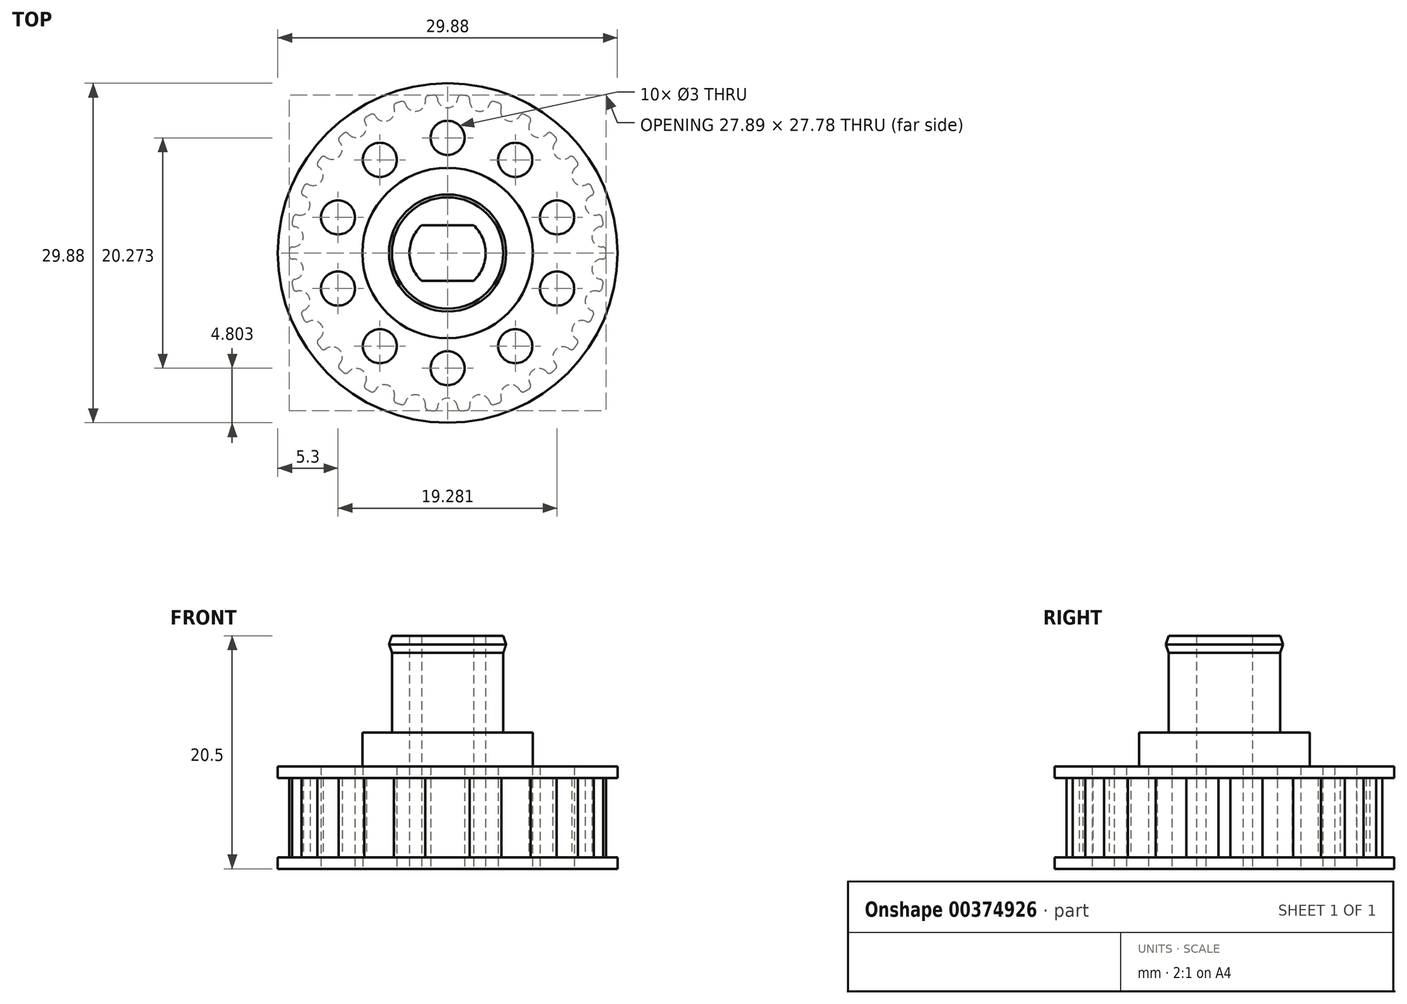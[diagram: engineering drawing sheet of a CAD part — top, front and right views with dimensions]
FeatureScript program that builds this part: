
annotation { "Feature Type Name" : "Feature", "Feature Type Description" : "" }
export const myFeature = defineFeature(function(context is Context, id is Id, definition is map)
    precondition{}
    {
        {
            assignVariable(context, id + "F0", {"name" : "e", "anyValue" : 3});
        }
        {
            assignVariable(context, id + "F1", {"name" : "h1", "anyValue" : 6});
        }
        {
            assignVariable(context, id + "F2", {"name" : "h2", "anyValue" : 6.5 + 5});
        }
        {
            var Q0;
            Q0=qCreatedBy(makeId("Top.planeOp"),FACE);
            var sketch = newSketch(context, id + "F3", { "sketchPlane" : qUnion([Q0])});
            skArc(sketch, "E0", {"start": v(-1.22, 13.89) * mm, "mid": v(0, -13.94) * mm, "end": v(1.22, 13.89) * mm, "construction": true});
            skCircle(sketch, "E1", {"center": v(0, 0) * mm, "radius": 7.5 * mm});
            skCircle(sketch, "E2", {"center": v(0, 0) * mm, "radius": 4.9 * mm});
            skArc(sketch, "E3", {"start": v(-2.28, 2.45) * mm, "mid": v(-3.35, 0) * mm, "end": v(-2.28, -2.45) * mm});
            skLineSegment(sketch, "E4.bottom", {"start": v(2.28, -2.45) * mm, "end": v(-2.28, -2.45) * mm});
            skLineSegment(sketch, "E4.top", {"start": v(2.28, 2.45) * mm, "end": v(-2.28, 2.45) * mm});
            skArc(sketch, "E5.trimOffspring", {"start": v(2.28, -2.45) * mm, "mid": v(3.35, 0) * mm, "end": v(2.28, 2.45) * mm});
            skPoint(sketch, "E6.orphan", {"position": v(3.35, 2.45) * mm});
            skPoint(sketch, "E7.orphan", {"position": v(3.35, -2.45) * mm});
            skPoint(sketch, "E8.orphan", {"position": v(-3.35, -2.45) * mm});
            skPoint(sketch, "E9.orphan", {"position": v(-3.35, 2.45) * mm});
            skLineSegment(sketch, "E10", {"start": v(0, 7.5) * mm, "end": v(0, 12.77) * mm, "construction": true});
            skCircle(sketch, "E11", {"center": v(0, 0) * mm, "radius": 14.94 * mm});
            skCircle(sketch, "E12", {"center": v(0, 10.14) * mm, "radius": 1.5 * mm});
            skCircle(sketch, "E13.1.0", {"center": v(-5.96, 8.2) * mm, "radius": 1.5 * mm});
            skCircle(sketch, "E13.2.0", {"center": v(-9.64, 3.13) * mm, "radius": 1.5 * mm});
            skCircle(sketch, "E13.3.0", {"center": v(-9.64, -3.13) * mm, "radius": 1.5 * mm});
            skCircle(sketch, "E13.4.0", {"center": v(-5.96, -8.2) * mm, "radius": 1.5 * mm});
            skCircle(sketch, "E13.5.0", {"center": v(0, -10.14) * mm, "radius": 1.5 * mm});
            skCircle(sketch, "E13.6.0", {"center": v(5.96, -8.2) * mm, "radius": 1.5 * mm});
            skCircle(sketch, "E13.7.0", {"center": v(9.64, -3.13) * mm, "radius": 1.5 * mm});
            skCircle(sketch, "E13.8.0", {"center": v(9.64, 3.13) * mm, "radius": 1.5 * mm});
            skCircle(sketch, "E13.9.0", {"center": v(5.96, 8.2) * mm, "radius": 1.5 * mm});
            skCircle(sketch, "E14", {"center": v(0, 0) * mm, "radius": 12.77 * mm, "construction": true});
            skLineSegment(sketch, "E15", {"start": v(0, 12.77) * mm, "end": v(0, 14.94) * mm});
            skArc(sketch, "E16", {"start": v(-0.9, 13.61) * mm, "mid": v(0, 12.77) * mm, "end": v(0.9, 13.61) * mm});
            skArc(sketch, "E17", {"start": v(1.22, 13.89) * mm, "mid": v(1, 13.82) * mm, "end": v(0.9, 13.61) * mm});
            skArc(sketch, "E18.MirrorCS", {"start": v(-1.22, 13.89) * mm, "mid": v(-1, 13.82) * mm, "end": v(-0.9, 13.61) * mm});
            skLineSegment(sketch, "E19", {"start": v(0, 0) * mm, "end": v(1.56, 14.86) * mm, "construction": true});
            skLineSegment(sketch, "E20", {"start": v(0, 0) * mm, "end": v(-1.56, 14.86) * mm, "construction": true});
            skArc(sketch, "E21", {"start": v(1.46, 13.87) * mm, "mid": v(1.34, 13.88) * mm, "end": v(1.22, 13.89) * mm});
            skArc(sketch, "E22.trimOffspring", {"start": v(-1.22, 13.89) * mm, "mid": v(-1.34, 13.88) * mm, "end": v(-1.46, 13.87) * mm});
            skArc(sketch, "E23.1.0", {"start": v(-4.08, 13.33) * mm, "mid": v(-4.2, 13.3) * mm, "end": v(-4.3, 13.26) * mm});
            skArc(sketch, "E23.1.1", {"start": v(-4.08, 13.33) * mm, "mid": v(-3.85, 13.3) * mm, "end": v(-3.7, 13.13) * mm});
            skArc(sketch, "E23.1.2", {"start": v(-3.7, 13.13) * mm, "mid": v(-2.66, 12.5) * mm, "end": v(-1.95, 13.5) * mm});
            skArc(sketch, "E23.1.3", {"start": v(-1.7, 13.84) * mm, "mid": v(-1.9, 13.72) * mm, "end": v(-1.95, 13.5) * mm});
            skArc(sketch, "E23.1.4", {"start": v(-1.46, 13.87) * mm, "mid": v(-1.57, 13.85) * mm, "end": v(-1.7, 13.84) * mm});
            skArc(sketch, "E23.2.0", {"start": v(-6.77, 12.2) * mm, "mid": v(-6.87, 12.13) * mm, "end": v(-6.97, 12.07) * mm});
            skArc(sketch, "E23.2.1", {"start": v(-6.77, 12.2) * mm, "mid": v(-6.54, 12.22) * mm, "end": v(-6.36, 12.07) * mm});
            skArc(sketch, "E23.2.2", {"start": v(-6.36, 12.07) * mm, "mid": v(-5.2, 11.67) * mm, "end": v(-4.72, 12.8) * mm});
            skArc(sketch, "E23.2.3", {"start": v(-4.53, 13.19) * mm, "mid": v(-4.7, 13.03) * mm, "end": v(-4.72, 12.8) * mm});
            skArc(sketch, "E23.2.4", {"start": v(-4.3, 13.26) * mm, "mid": v(-4.42, 13.22) * mm, "end": v(-4.53, 13.19) * mm});
            skArc(sketch, "E23.3.0", {"start": v(-9.15, 10.52) * mm, "mid": v(-9.24, 10.44) * mm, "end": v(-9.33, 10.36) * mm});
            skArc(sketch, "E23.3.1", {"start": v(-9.15, 10.52) * mm, "mid": v(-8.93, 10.6) * mm, "end": v(-8.73, 10.48) * mm});
            skArc(sketch, "E23.3.2", {"start": v(-8.73, 10.48) * mm, "mid": v(-7.5, 10.33) * mm, "end": v(-7.27, 11.54) * mm});
            skArc(sketch, "E23.3.3", {"start": v(-7.17, 11.96) * mm, "mid": v(-7.31, 11.77) * mm, "end": v(-7.27, 11.54) * mm});
            skArc(sketch, "E23.3.4", {"start": v(-6.97, 12.07) * mm, "mid": v(-7.07, 12.02) * mm, "end": v(-7.17, 11.96) * mm});
            skArc(sketch, "E23.4.0", {"start": v(-11.14, 8.38) * mm, "mid": v(-11.21, 8.3) * mm, "end": v(-11.28, 8.2) * mm});
            skArc(sketch, "E23.4.1", {"start": v(-11.14, 8.38) * mm, "mid": v(-10.94, 8.5) * mm, "end": v(-10.72, 8.44) * mm});
            skArc(sketch, "E23.4.2", {"start": v(-10.72, 8.44) * mm, "mid": v(-9.5, 8.55) * mm, "end": v(-9.51, 9.77) * mm});
            skArc(sketch, "E23.4.3", {"start": v(-9.5, 10.2) * mm, "mid": v(-9.6, 10) * mm, "end": v(-9.51, 9.77) * mm});
            skArc(sketch, "E23.4.4", {"start": v(-9.33, 10.36) * mm, "mid": v(-9.42, 10.28) * mm, "end": v(-9.5, 10.2) * mm});
            skArc(sketch, "E23.5.0", {"start": v(-12.64, 5.89) * mm, "mid": v(-12.69, 5.78) * mm, "end": v(-12.74, 5.67) * mm});
            skArc(sketch, "E23.5.1", {"start": v(-12.64, 5.89) * mm, "mid": v(-12.47, 6.04) * mm, "end": v(-12.24, 6.03) * mm});
            skArc(sketch, "E23.5.2", {"start": v(-12.24, 6.03) * mm, "mid": v(-11.06, 6.39) * mm, "end": v(-11.34, 7.58) * mm});
            skArc(sketch, "E23.5.3", {"start": v(-11.42, 8) * mm, "mid": v(-11.47, 7.78) * mm, "end": v(-11.34, 7.58) * mm});
            skArc(sketch, "E23.5.4", {"start": v(-11.28, 8.2) * mm, "mid": v(-11.35, 8.1) * mm, "end": v(-11.42, 8) * mm});
            skArc(sketch, "E23.6.0", {"start": v(-13.59, 3.13) * mm, "mid": v(-13.61, 3.01) * mm, "end": v(-13.64, 2.9) * mm});
            skArc(sketch, "E23.6.1", {"start": v(-13.59, 3.13) * mm, "mid": v(-13.45, 3.32) * mm, "end": v(-13.22, 3.35) * mm});
            skArc(sketch, "E23.6.2", {"start": v(-13.22, 3.35) * mm, "mid": v(-12.15, 3.95) * mm, "end": v(-12.67, 5.06) * mm});
            skArc(sketch, "E23.6.3", {"start": v(-12.83, 5.46) * mm, "mid": v(-12.83, 5.22) * mm, "end": v(-12.67, 5.06) * mm});
            skArc(sketch, "E23.6.4", {"start": v(-12.74, 5.67) * mm, "mid": v(-12.78, 5.56) * mm, "end": v(-12.83, 5.46) * mm});
            skArc(sketch, "E23.7.0", {"start": v(-13.94, 0.24) * mm, "mid": v(-13.94, 0.12) * mm, "end": v(-13.94, 0) * mm});
            skArc(sketch, "E23.7.1", {"start": v(-13.94, 0.24) * mm, "mid": v(-13.85, 0.45) * mm, "end": v(-13.63, 0.53) * mm});
            skArc(sketch, "E23.7.2", {"start": v(-13.63, 0.53) * mm, "mid": v(-12.7, 1.34) * mm, "end": v(-13.44, 2.32) * mm});
            skArc(sketch, "E23.7.3", {"start": v(-13.69, 2.67) * mm, "mid": v(-13.64, 2.44) * mm, "end": v(-13.44, 2.32) * mm});
            skArc(sketch, "E23.7.4", {"start": v(-13.64, 2.9) * mm, "mid": v(-13.66, 2.78) * mm, "end": v(-13.69, 2.67) * mm});
            skArc(sketch, "E23.8.0", {"start": v(-13.69, -2.67) * mm, "mid": v(-13.66, -2.78) * mm, "end": v(-13.64, -2.9) * mm});
            skArc(sketch, "E23.8.1", {"start": v(-13.69, -2.67) * mm, "mid": v(-13.64, -2.44) * mm, "end": v(-13.44, -2.32) * mm});
            skArc(sketch, "E23.8.2", {"start": v(-13.44, -2.32) * mm, "mid": v(-12.7, -1.34) * mm, "end": v(-13.63, -0.53) * mm});
            skArc(sketch, "E23.8.3", {"start": v(-13.94, -0.24) * mm, "mid": v(-13.85, -0.45) * mm, "end": v(-13.63, -0.53) * mm});
            skArc(sketch, "E23.8.4", {"start": v(-13.94, 0) * mm, "mid": v(-13.94, -0.12) * mm, "end": v(-13.94, -0.24) * mm});
            skArc(sketch, "E23.9.0", {"start": v(-12.83, -5.46) * mm, "mid": v(-12.78, -5.56) * mm, "end": v(-12.74, -5.67) * mm});
            skArc(sketch, "E23.9.1", {"start": v(-12.83, -5.46) * mm, "mid": v(-12.83, -5.22) * mm, "end": v(-12.67, -5.06) * mm});
            skArc(sketch, "E23.9.2", {"start": v(-12.67, -5.06) * mm, "mid": v(-12.15, -3.95) * mm, "end": v(-13.22, -3.35) * mm});
            skArc(sketch, "E23.9.3", {"start": v(-13.59, -3.13) * mm, "mid": v(-13.45, -3.32) * mm, "end": v(-13.22, -3.35) * mm});
            skArc(sketch, "E23.9.4", {"start": v(-13.64, -2.9) * mm, "mid": v(-13.61, -3.01) * mm, "end": v(-13.59, -3.13) * mm});
            skArc(sketch, "E23.10.0", {"start": v(-11.42, -8) * mm, "mid": v(-11.35, -8.1) * mm, "end": v(-11.28, -8.2) * mm});
            skArc(sketch, "E23.10.1", {"start": v(-11.42, -8) * mm, "mid": v(-11.47, -7.78) * mm, "end": v(-11.34, -7.58) * mm});
            skArc(sketch, "E23.10.2", {"start": v(-11.34, -7.58) * mm, "mid": v(-11.06, -6.39) * mm, "end": v(-12.24, -6.03) * mm});
            skArc(sketch, "E23.10.3", {"start": v(-12.64, -5.89) * mm, "mid": v(-12.47, -6.04) * mm, "end": v(-12.24, -6.03) * mm});
            skArc(sketch, "E23.10.4", {"start": v(-12.74, -5.67) * mm, "mid": v(-12.69, -5.78) * mm, "end": v(-12.64, -5.89) * mm});
            skArc(sketch, "E23.11.0", {"start": v(-9.5, -10.2) * mm, "mid": v(-9.42, -10.28) * mm, "end": v(-9.33, -10.36) * mm});
            skArc(sketch, "E23.11.1", {"start": v(-9.5, -10.2) * mm, "mid": v(-9.6, -10) * mm, "end": v(-9.51, -9.77) * mm});
            skArc(sketch, "E23.11.2", {"start": v(-9.51, -9.77) * mm, "mid": v(-9.5, -8.55) * mm, "end": v(-10.72, -8.44) * mm});
            skArc(sketch, "E23.11.3", {"start": v(-11.14, -8.38) * mm, "mid": v(-10.94, -8.5) * mm, "end": v(-10.72, -8.44) * mm});
            skArc(sketch, "E23.11.4", {"start": v(-11.28, -8.2) * mm, "mid": v(-11.21, -8.3) * mm, "end": v(-11.14, -8.38) * mm});
            skArc(sketch, "E23.12.0", {"start": v(-7.17, -11.96) * mm, "mid": v(-7.07, -12.02) * mm, "end": v(-6.97, -12.07) * mm});
            skArc(sketch, "E23.12.1", {"start": v(-7.17, -11.96) * mm, "mid": v(-7.31, -11.77) * mm, "end": v(-7.27, -11.54) * mm});
            skArc(sketch, "E23.12.2", {"start": v(-7.27, -11.54) * mm, "mid": v(-7.5, -10.33) * mm, "end": v(-8.73, -10.48) * mm});
            skArc(sketch, "E23.12.3", {"start": v(-9.15, -10.52) * mm, "mid": v(-8.93, -10.6) * mm, "end": v(-8.73, -10.48) * mm});
            skArc(sketch, "E23.12.4", {"start": v(-9.33, -10.36) * mm, "mid": v(-9.24, -10.44) * mm, "end": v(-9.15, -10.52) * mm});
            skArc(sketch, "E23.13.0", {"start": v(-4.53, -13.19) * mm, "mid": v(-4.42, -13.22) * mm, "end": v(-4.3, -13.26) * mm});
            skArc(sketch, "E23.13.1", {"start": v(-4.53, -13.19) * mm, "mid": v(-4.7, -13.03) * mm, "end": v(-4.72, -12.8) * mm});
            skArc(sketch, "E23.13.2", {"start": v(-4.72, -12.8) * mm, "mid": v(-5.2, -11.67) * mm, "end": v(-6.36, -12.07) * mm});
            skArc(sketch, "E23.13.3", {"start": v(-6.77, -12.2) * mm, "mid": v(-6.54, -12.22) * mm, "end": v(-6.36, -12.07) * mm});
            skArc(sketch, "E23.13.4", {"start": v(-6.97, -12.07) * mm, "mid": v(-6.87, -12.13) * mm, "end": v(-6.77, -12.2) * mm});
            skArc(sketch, "E23.14.0", {"start": v(-1.7, -13.84) * mm, "mid": v(-1.57, -13.85) * mm, "end": v(-1.46, -13.87) * mm});
            skArc(sketch, "E23.14.1", {"start": v(-1.7, -13.84) * mm, "mid": v(-1.9, -13.72) * mm, "end": v(-1.95, -13.5) * mm});
            skArc(sketch, "E23.14.2", {"start": v(-1.95, -13.5) * mm, "mid": v(-2.66, -12.5) * mm, "end": v(-3.7, -13.13) * mm});
            skArc(sketch, "E23.14.3", {"start": v(-4.08, -13.33) * mm, "mid": v(-3.85, -13.3) * mm, "end": v(-3.7, -13.13) * mm});
            skArc(sketch, "E23.14.4", {"start": v(-4.3, -13.26) * mm, "mid": v(-4.2, -13.3) * mm, "end": v(-4.08, -13.33) * mm});
            skArc(sketch, "E23.15.0", {"start": v(1.22, -13.89) * mm, "mid": v(1.34, -13.88) * mm, "end": v(1.46, -13.87) * mm});
            skArc(sketch, "E23.15.1", {"start": v(1.22, -13.89) * mm, "mid": v(1, -13.82) * mm, "end": v(0.9, -13.61) * mm});
            skArc(sketch, "E23.15.2", {"start": v(0.9, -13.61) * mm, "mid": v(0, -12.77) * mm, "end": v(-0.9, -13.61) * mm});
            skArc(sketch, "E23.15.3", {"start": v(-1.22, -13.89) * mm, "mid": v(-1, -13.82) * mm, "end": v(-0.9, -13.61) * mm});
            skArc(sketch, "E23.15.4", {"start": v(-1.46, -13.87) * mm, "mid": v(-1.34, -13.88) * mm, "end": v(-1.22, -13.89) * mm});
            skArc(sketch, "E23.16.0", {"start": v(4.08, -13.33) * mm, "mid": v(4.2, -13.3) * mm, "end": v(4.3, -13.26) * mm});
            skArc(sketch, "E23.16.1", {"start": v(4.08, -13.33) * mm, "mid": v(3.85, -13.3) * mm, "end": v(3.7, -13.13) * mm});
            skArc(sketch, "E23.16.2", {"start": v(3.7, -13.13) * mm, "mid": v(2.66, -12.5) * mm, "end": v(1.95, -13.5) * mm});
            skArc(sketch, "E23.16.3", {"start": v(1.7, -13.84) * mm, "mid": v(1.9, -13.72) * mm, "end": v(1.95, -13.5) * mm});
            skArc(sketch, "E23.16.4", {"start": v(1.46, -13.87) * mm, "mid": v(1.57, -13.85) * mm, "end": v(1.7, -13.84) * mm});
            skArc(sketch, "E23.17.0", {"start": v(6.77, -12.2) * mm, "mid": v(6.87, -12.13) * mm, "end": v(6.97, -12.07) * mm});
            skArc(sketch, "E23.17.1", {"start": v(6.77, -12.2) * mm, "mid": v(6.54, -12.22) * mm, "end": v(6.36, -12.07) * mm});
            skArc(sketch, "E23.17.2", {"start": v(6.36, -12.07) * mm, "mid": v(5.2, -11.67) * mm, "end": v(4.72, -12.8) * mm});
            skArc(sketch, "E23.17.3", {"start": v(4.53, -13.19) * mm, "mid": v(4.7, -13.03) * mm, "end": v(4.72, -12.8) * mm});
            skArc(sketch, "E23.17.4", {"start": v(4.3, -13.26) * mm, "mid": v(4.42, -13.22) * mm, "end": v(4.53, -13.19) * mm});
            skArc(sketch, "E23.18.0", {"start": v(9.15, -10.52) * mm, "mid": v(9.24, -10.44) * mm, "end": v(9.33, -10.36) * mm});
            skArc(sketch, "E23.18.1", {"start": v(9.15, -10.52) * mm, "mid": v(8.93, -10.6) * mm, "end": v(8.73, -10.48) * mm});
            skArc(sketch, "E23.18.2", {"start": v(8.73, -10.48) * mm, "mid": v(7.5, -10.33) * mm, "end": v(7.27, -11.54) * mm});
            skArc(sketch, "E23.18.3", {"start": v(7.17, -11.96) * mm, "mid": v(7.31, -11.77) * mm, "end": v(7.27, -11.54) * mm});
            skArc(sketch, "E23.18.4", {"start": v(6.97, -12.07) * mm, "mid": v(7.07, -12.02) * mm, "end": v(7.17, -11.96) * mm});
            skArc(sketch, "E23.19.0", {"start": v(11.14, -8.38) * mm, "mid": v(11.21, -8.3) * mm, "end": v(11.28, -8.2) * mm});
            skArc(sketch, "E23.19.1", {"start": v(11.14, -8.38) * mm, "mid": v(10.94, -8.5) * mm, "end": v(10.72, -8.44) * mm});
            skArc(sketch, "E23.19.2", {"start": v(10.72, -8.44) * mm, "mid": v(9.5, -8.55) * mm, "end": v(9.51, -9.77) * mm});
            skArc(sketch, "E23.19.3", {"start": v(9.5, -10.2) * mm, "mid": v(9.6, -10) * mm, "end": v(9.51, -9.77) * mm});
            skArc(sketch, "E23.19.4", {"start": v(9.33, -10.36) * mm, "mid": v(9.42, -10.28) * mm, "end": v(9.5, -10.2) * mm});
            skArc(sketch, "E23.20.0", {"start": v(12.64, -5.89) * mm, "mid": v(12.69, -5.78) * mm, "end": v(12.74, -5.67) * mm});
            skArc(sketch, "E23.20.1", {"start": v(12.64, -5.89) * mm, "mid": v(12.47, -6.04) * mm, "end": v(12.24, -6.03) * mm});
            skArc(sketch, "E23.20.2", {"start": v(12.24, -6.03) * mm, "mid": v(11.06, -6.39) * mm, "end": v(11.34, -7.58) * mm});
            skArc(sketch, "E23.20.3", {"start": v(11.42, -8) * mm, "mid": v(11.47, -7.78) * mm, "end": v(11.34, -7.58) * mm});
            skArc(sketch, "E23.20.4", {"start": v(11.28, -8.2) * mm, "mid": v(11.35, -8.1) * mm, "end": v(11.42, -8) * mm});
            skArc(sketch, "E23.21.0", {"start": v(13.59, -3.13) * mm, "mid": v(13.61, -3.01) * mm, "end": v(13.64, -2.9) * mm});
            skArc(sketch, "E23.21.1", {"start": v(13.59, -3.13) * mm, "mid": v(13.45, -3.32) * mm, "end": v(13.22, -3.35) * mm});
            skArc(sketch, "E23.21.2", {"start": v(13.22, -3.35) * mm, "mid": v(12.15, -3.95) * mm, "end": v(12.67, -5.06) * mm});
            skArc(sketch, "E23.21.3", {"start": v(12.83, -5.46) * mm, "mid": v(12.83, -5.22) * mm, "end": v(12.67, -5.06) * mm});
            skArc(sketch, "E23.21.4", {"start": v(12.74, -5.67) * mm, "mid": v(12.78, -5.56) * mm, "end": v(12.83, -5.46) * mm});
            skArc(sketch, "E23.22.0", {"start": v(13.94, -0.24) * mm, "mid": v(13.94, -0.12) * mm, "end": v(13.94, 0) * mm});
            skArc(sketch, "E23.22.1", {"start": v(13.94, -0.24) * mm, "mid": v(13.85, -0.45) * mm, "end": v(13.63, -0.53) * mm});
            skArc(sketch, "E23.22.2", {"start": v(13.63, -0.53) * mm, "mid": v(12.7, -1.34) * mm, "end": v(13.44, -2.32) * mm});
            skArc(sketch, "E23.22.3", {"start": v(13.69, -2.67) * mm, "mid": v(13.64, -2.44) * mm, "end": v(13.44, -2.32) * mm});
            skArc(sketch, "E23.22.4", {"start": v(13.64, -2.9) * mm, "mid": v(13.66, -2.78) * mm, "end": v(13.69, -2.67) * mm});
            skArc(sketch, "E23.23.0", {"start": v(13.69, 2.67) * mm, "mid": v(13.66, 2.78) * mm, "end": v(13.64, 2.9) * mm});
            skArc(sketch, "E23.23.1", {"start": v(13.69, 2.67) * mm, "mid": v(13.64, 2.44) * mm, "end": v(13.44, 2.32) * mm});
            skArc(sketch, "E23.23.2", {"start": v(13.44, 2.32) * mm, "mid": v(12.7, 1.34) * mm, "end": v(13.63, 0.53) * mm});
            skArc(sketch, "E23.23.3", {"start": v(13.94, 0.24) * mm, "mid": v(13.85, 0.45) * mm, "end": v(13.63, 0.53) * mm});
            skArc(sketch, "E23.23.4", {"start": v(13.94, 0) * mm, "mid": v(13.94, 0.12) * mm, "end": v(13.94, 0.24) * mm});
            skArc(sketch, "E23.24.0", {"start": v(12.83, 5.46) * mm, "mid": v(12.78, 5.56) * mm, "end": v(12.74, 5.67) * mm});
            skArc(sketch, "E23.24.1", {"start": v(12.83, 5.46) * mm, "mid": v(12.83, 5.22) * mm, "end": v(12.67, 5.06) * mm});
            skArc(sketch, "E23.24.2", {"start": v(12.67, 5.06) * mm, "mid": v(12.15, 3.95) * mm, "end": v(13.22, 3.35) * mm});
            skArc(sketch, "E23.24.3", {"start": v(13.59, 3.13) * mm, "mid": v(13.45, 3.32) * mm, "end": v(13.22, 3.35) * mm});
            skArc(sketch, "E23.24.4", {"start": v(13.64, 2.9) * mm, "mid": v(13.61, 3.01) * mm, "end": v(13.59, 3.13) * mm});
            skArc(sketch, "E23.25.0", {"start": v(11.42, 8) * mm, "mid": v(11.35, 8.1) * mm, "end": v(11.28, 8.2) * mm});
            skArc(sketch, "E23.25.1", {"start": v(11.42, 8) * mm, "mid": v(11.47, 7.78) * mm, "end": v(11.34, 7.58) * mm});
            skArc(sketch, "E23.25.2", {"start": v(11.34, 7.58) * mm, "mid": v(11.06, 6.39) * mm, "end": v(12.24, 6.03) * mm});
            skArc(sketch, "E23.25.3", {"start": v(12.64, 5.89) * mm, "mid": v(12.47, 6.04) * mm, "end": v(12.24, 6.03) * mm});
            skArc(sketch, "E23.25.4", {"start": v(12.74, 5.67) * mm, "mid": v(12.69, 5.78) * mm, "end": v(12.64, 5.89) * mm});
            skArc(sketch, "E23.26.0", {"start": v(9.5, 10.2) * mm, "mid": v(9.42, 10.28) * mm, "end": v(9.33, 10.36) * mm});
            skArc(sketch, "E23.26.1", {"start": v(9.5, 10.2) * mm, "mid": v(9.6, 10) * mm, "end": v(9.51, 9.77) * mm});
            skArc(sketch, "E23.26.2", {"start": v(9.51, 9.77) * mm, "mid": v(9.5, 8.55) * mm, "end": v(10.72, 8.44) * mm});
            skArc(sketch, "E23.26.3", {"start": v(11.14, 8.38) * mm, "mid": v(10.94, 8.5) * mm, "end": v(10.72, 8.44) * mm});
            skArc(sketch, "E23.26.4", {"start": v(11.28, 8.2) * mm, "mid": v(11.21, 8.3) * mm, "end": v(11.14, 8.38) * mm});
            skArc(sketch, "E23.27.0", {"start": v(7.17, 11.96) * mm, "mid": v(7.07, 12.02) * mm, "end": v(6.97, 12.07) * mm});
            skArc(sketch, "E23.27.1", {"start": v(7.17, 11.96) * mm, "mid": v(7.31, 11.77) * mm, "end": v(7.27, 11.54) * mm});
            skArc(sketch, "E23.27.2", {"start": v(7.27, 11.54) * mm, "mid": v(7.5, 10.33) * mm, "end": v(8.73, 10.48) * mm});
            skArc(sketch, "E23.27.3", {"start": v(9.15, 10.52) * mm, "mid": v(8.93, 10.6) * mm, "end": v(8.73, 10.48) * mm});
            skArc(sketch, "E23.27.4", {"start": v(9.33, 10.36) * mm, "mid": v(9.24, 10.44) * mm, "end": v(9.15, 10.52) * mm});
            skArc(sketch, "E23.28.0", {"start": v(4.53, 13.19) * mm, "mid": v(4.42, 13.22) * mm, "end": v(4.3, 13.26) * mm});
            skArc(sketch, "E23.28.1", {"start": v(4.53, 13.19) * mm, "mid": v(4.7, 13.03) * mm, "end": v(4.72, 12.8) * mm});
            skArc(sketch, "E23.28.2", {"start": v(4.72, 12.8) * mm, "mid": v(5.2, 11.67) * mm, "end": v(6.36, 12.07) * mm});
            skArc(sketch, "E23.28.3", {"start": v(6.77, 12.2) * mm, "mid": v(6.54, 12.22) * mm, "end": v(6.36, 12.07) * mm});
            skArc(sketch, "E23.28.4", {"start": v(6.97, 12.07) * mm, "mid": v(6.87, 12.13) * mm, "end": v(6.77, 12.2) * mm});
            skArc(sketch, "E23.29.0", {"start": v(1.7, 13.84) * mm, "mid": v(1.57, 13.85) * mm, "end": v(1.46, 13.87) * mm});
            skArc(sketch, "E23.29.1", {"start": v(1.7, 13.84) * mm, "mid": v(1.9, 13.72) * mm, "end": v(1.95, 13.5) * mm});
            skArc(sketch, "E23.29.2", {"start": v(1.95, 13.5) * mm, "mid": v(2.66, 12.5) * mm, "end": v(3.7, 13.13) * mm});
            skArc(sketch, "E23.29.3", {"start": v(4.08, 13.33) * mm, "mid": v(3.85, 13.3) * mm, "end": v(3.7, 13.13) * mm});
            skArc(sketch, "E23.29.4", {"start": v(4.3, 13.26) * mm, "mid": v(4.2, 13.3) * mm, "end": v(4.08, 13.33) * mm});
            skSolve(sketch);
        }
        {
            var Q0;
            Q0=makeQuery(id+"F3.imprint","IMPRINT",FACE,{"disambiguationData":[TD([[makeQuery(id+"F3.imprint","IMPRINT",EDGE,{"derivedFrom":sQuery(id+"F3.wireOp",EDGE,"E1")}),-1.0]])]});
            var Q1;
            Q1=makeQuery(id+"F3.imprint","IMPRINT",FACE,{"disambiguationData":[TD([[makeQuery(id+"F3.imprint","IMPRINT",EDGE,{"derivedFrom":sQuery(id+"F3.wireOp",EDGE,"E1")}),1.0]])]});
            var Q2;
            Q2=makeQuery(id+"F3.imprint","IMPRINT",FACE,{"disambiguationData":[TD([[makeQuery(id+"F3.imprint","IMPRINT",EDGE,{"derivedFrom":sQuery(id+"F3.wireOp",EDGE,"E2")}),1.0]])]});
            extrude(context, id + "F4", {"entities" : qUnion([Q0, Q1, Q2]), "depth" : 8 * mm});
        }
        {
            var Q0;
            Q0=makeQuery(id+"F3.imprint","IMPRINT",FACE,{"disambiguationData":[TD([[makeQuery(id+"F3.imprint","IMPRINT",EDGE,{"derivedFrom":sQuery(id+"F3.wireOp",EDGE,"E11")}),1.0]])]});
            var Q1;
            Q1=makeQuery(id+"F3.imprint","IMPRINT",FACE,{"disambiguationData":[TD([[makeQuery(id+"F3.imprint","IMPRINT",EDGE,{"derivedFrom":sQuery(id+"F3.wireOp",EDGE,"E1")}),-1.0]])]});
            var Q2;
            Q2=makeQuery(id+"F3.imprint","IMPRINT",FACE,{"disambiguationData":[TD([[makeQuery(id+"F3.imprint","IMPRINT",EDGE,{"derivedFrom":sQuery(id+"F3.wireOp",EDGE,"E1")}),1.0]])]});
            var Q3;
            Q3=makeQuery(id+"F3.imprint","IMPRINT",FACE,{"disambiguationData":[TD([[makeQuery(id+"F3.imprint","IMPRINT",EDGE,{"derivedFrom":sQuery(id+"F3.wireOp",EDGE,"E2")}),1.0]])]});
            extrude(context, id + "F5", {"entities" : qUnion([Q0, Q1, Q2, Q3]), "depth" : 1 * mm});
        }
        {
            var Q0;
            Q0=makeQuery(id+"F5.opExtrude","SWEPT_BODY",BODY,{"disambiguationData":[OSD([sQuery(id+"F3.wireOp",EDGE,"E11"),sQuery(id+"F3.wireOp",EDGE,"E16"),sQuery(id+"F3.wireOp",EDGE,"E17"),sQuery(id+"F3.wireOp",EDGE,"E18.MirrorCS"),sQuery(id+"F3.wireOp",EDGE,"E21"),sQuery(id+"F3.wireOp",EDGE,"E22.trimOffspring"),sQuery(id+"F3.wireOp",EDGE,"E23.1.0"),sQuery(id+"F3.wireOp",EDGE,"E23.1.1"),sQuery(id+"F3.wireOp",EDGE,"E23.1.2"),sQuery(id+"F3.wireOp",EDGE,"E23.1.3"),sQuery(id+"F3.wireOp",EDGE,"E23.1.4"),sQuery(id+"F3.wireOp",EDGE,"E23.2.0"),sQuery(id+"F3.wireOp",EDGE,"E23.2.1"),sQuery(id+"F3.wireOp",EDGE,"E23.2.2"),sQuery(id+"F3.wireOp",EDGE,"E23.2.3"),sQuery(id+"F3.wireOp",EDGE,"E23.2.4"),sQuery(id+"F3.wireOp",EDGE,"E23.3.0"),sQuery(id+"F3.wireOp",EDGE,"E23.3.1"),sQuery(id+"F3.wireOp",EDGE,"E23.3.2"),sQuery(id+"F3.wireOp",EDGE,"E23.3.3"),sQuery(id+"F3.wireOp",EDGE,"E23.3.4"),sQuery(id+"F3.wireOp",EDGE,"E23.4.0"),sQuery(id+"F3.wireOp",EDGE,"E23.4.1"),sQuery(id+"F3.wireOp",EDGE,"E23.4.2"),sQuery(id+"F3.wireOp",EDGE,"E23.4.3"),sQuery(id+"F3.wireOp",EDGE,"E23.4.4"),sQuery(id+"F3.wireOp",EDGE,"E23.5.0"),sQuery(id+"F3.wireOp",EDGE,"E23.5.1"),sQuery(id+"F3.wireOp",EDGE,"E23.5.2"),sQuery(id+"F3.wireOp",EDGE,"E23.5.3"),sQuery(id+"F3.wireOp",EDGE,"E23.5.4"),sQuery(id+"F3.wireOp",EDGE,"E23.6.0"),sQuery(id+"F3.wireOp",EDGE,"E23.6.1"),sQuery(id+"F3.wireOp",EDGE,"E23.6.2"),sQuery(id+"F3.wireOp",EDGE,"E23.6.3"),sQuery(id+"F3.wireOp",EDGE,"E23.6.4"),sQuery(id+"F3.wireOp",EDGE,"E23.7.0"),sQuery(id+"F3.wireOp",EDGE,"E23.7.1"),sQuery(id+"F3.wireOp",EDGE,"E23.7.2"),sQuery(id+"F3.wireOp",EDGE,"E23.7.3"),sQuery(id+"F3.wireOp",EDGE,"E23.7.4"),sQuery(id+"F3.wireOp",EDGE,"E23.8.0"),sQuery(id+"F3.wireOp",EDGE,"E23.8.1"),sQuery(id+"F3.wireOp",EDGE,"E23.8.2"),sQuery(id+"F3.wireOp",EDGE,"E23.8.3"),sQuery(id+"F3.wireOp",EDGE,"E23.8.4"),sQuery(id+"F3.wireOp",EDGE,"E23.9.0"),sQuery(id+"F3.wireOp",EDGE,"E23.9.1"),sQuery(id+"F3.wireOp",EDGE,"E23.9.2"),sQuery(id+"F3.wireOp",EDGE,"E23.9.3"),sQuery(id+"F3.wireOp",EDGE,"E23.9.4"),sQuery(id+"F3.wireOp",EDGE,"E23.10.0"),sQuery(id+"F3.wireOp",EDGE,"E23.10.1"),sQuery(id+"F3.wireOp",EDGE,"E23.10.2"),sQuery(id+"F3.wireOp",EDGE,"E23.10.3"),sQuery(id+"F3.wireOp",EDGE,"E23.10.4"),sQuery(id+"F3.wireOp",EDGE,"E23.11.0"),sQuery(id+"F3.wireOp",EDGE,"E23.11.1"),sQuery(id+"F3.wireOp",EDGE,"E23.11.2"),sQuery(id+"F3.wireOp",EDGE,"E23.11.3"),sQuery(id+"F3.wireOp",EDGE,"E23.11.4"),sQuery(id+"F3.wireOp",EDGE,"E23.12.0"),sQuery(id+"F3.wireOp",EDGE,"E23.12.1"),sQuery(id+"F3.wireOp",EDGE,"E23.12.2"),sQuery(id+"F3.wireOp",EDGE,"E23.12.3"),sQuery(id+"F3.wireOp",EDGE,"E23.12.4"),sQuery(id+"F3.wireOp",EDGE,"E23.13.0"),sQuery(id+"F3.wireOp",EDGE,"E23.13.1"),sQuery(id+"F3.wireOp",EDGE,"E23.13.2"),sQuery(id+"F3.wireOp",EDGE,"E23.13.3"),sQuery(id+"F3.wireOp",EDGE,"E23.13.4"),sQuery(id+"F3.wireOp",EDGE,"E23.14.0"),sQuery(id+"F3.wireOp",EDGE,"E23.14.1"),sQuery(id+"F3.wireOp",EDGE,"E23.14.2"),sQuery(id+"F3.wireOp",EDGE,"E23.14.3"),sQuery(id+"F3.wireOp",EDGE,"E23.14.4"),sQuery(id+"F3.wireOp",EDGE,"E23.15.0"),sQuery(id+"F3.wireOp",EDGE,"E23.15.1"),sQuery(id+"F3.wireOp",EDGE,"E23.15.2"),sQuery(id+"F3.wireOp",EDGE,"E23.15.3"),sQuery(id+"F3.wireOp",EDGE,"E23.15.4"),sQuery(id+"F3.wireOp",EDGE,"E23.16.0"),sQuery(id+"F3.wireOp",EDGE,"E23.16.1"),sQuery(id+"F3.wireOp",EDGE,"E23.16.2"),sQuery(id+"F3.wireOp",EDGE,"E23.16.3"),sQuery(id+"F3.wireOp",EDGE,"E23.16.4"),sQuery(id+"F3.wireOp",EDGE,"E23.17.0"),sQuery(id+"F3.wireOp",EDGE,"E23.17.1"),sQuery(id+"F3.wireOp",EDGE,"E23.17.2"),sQuery(id+"F3.wireOp",EDGE,"E23.17.3"),sQuery(id+"F3.wireOp",EDGE,"E23.17.4"),sQuery(id+"F3.wireOp",EDGE,"E23.18.0"),sQuery(id+"F3.wireOp",EDGE,"E23.18.1"),sQuery(id+"F3.wireOp",EDGE,"E23.18.2"),sQuery(id+"F3.wireOp",EDGE,"E23.18.3"),sQuery(id+"F3.wireOp",EDGE,"E23.18.4"),sQuery(id+"F3.wireOp",EDGE,"E23.19.0"),sQuery(id+"F3.wireOp",EDGE,"E23.19.1"),sQuery(id+"F3.wireOp",EDGE,"E23.19.2"),sQuery(id+"F3.wireOp",EDGE,"E23.19.3"),sQuery(id+"F3.wireOp",EDGE,"E23.19.4"),sQuery(id+"F3.wireOp",EDGE,"E23.20.0"),sQuery(id+"F3.wireOp",EDGE,"E23.20.1"),sQuery(id+"F3.wireOp",EDGE,"E23.20.2"),sQuery(id+"F3.wireOp",EDGE,"E23.20.3"),sQuery(id+"F3.wireOp",EDGE,"E23.20.4"),sQuery(id+"F3.wireOp",EDGE,"E23.21.0"),sQuery(id+"F3.wireOp",EDGE,"E23.21.1"),sQuery(id+"F3.wireOp",EDGE,"E23.21.2"),sQuery(id+"F3.wireOp",EDGE,"E23.21.3"),sQuery(id+"F3.wireOp",EDGE,"E23.21.4"),sQuery(id+"F3.wireOp",EDGE,"E23.22.0"),sQuery(id+"F3.wireOp",EDGE,"E23.22.1"),sQuery(id+"F3.wireOp",EDGE,"E23.22.2"),sQuery(id+"F3.wireOp",EDGE,"E23.22.3"),sQuery(id+"F3.wireOp",EDGE,"E23.22.4"),sQuery(id+"F3.wireOp",EDGE,"E23.23.0"),sQuery(id+"F3.wireOp",EDGE,"E23.23.1"),sQuery(id+"F3.wireOp",EDGE,"E23.23.2"),sQuery(id+"F3.wireOp",EDGE,"E23.23.3"),sQuery(id+"F3.wireOp",EDGE,"E23.23.4"),sQuery(id+"F3.wireOp",EDGE,"E23.24.0"),sQuery(id+"F3.wireOp",EDGE,"E23.24.1"),sQuery(id+"F3.wireOp",EDGE,"E23.24.2"),sQuery(id+"F3.wireOp",EDGE,"E23.24.3"),sQuery(id+"F3.wireOp",EDGE,"E23.24.4"),sQuery(id+"F3.wireOp",EDGE,"E23.25.0"),sQuery(id+"F3.wireOp",EDGE,"E23.25.1"),sQuery(id+"F3.wireOp",EDGE,"E23.25.2"),sQuery(id+"F3.wireOp",EDGE,"E23.25.3"),sQuery(id+"F3.wireOp",EDGE,"E23.25.4"),sQuery(id+"F3.wireOp",EDGE,"E23.26.0"),sQuery(id+"F3.wireOp",EDGE,"E23.26.1"),sQuery(id+"F3.wireOp",EDGE,"E23.26.2"),sQuery(id+"F3.wireOp",EDGE,"E23.26.3"),sQuery(id+"F3.wireOp",EDGE,"E23.26.4"),sQuery(id+"F3.wireOp",EDGE,"E23.27.0"),sQuery(id+"F3.wireOp",EDGE,"E23.27.1"),sQuery(id+"F3.wireOp",EDGE,"E23.27.2"),sQuery(id+"F3.wireOp",EDGE,"E23.27.3"),sQuery(id+"F3.wireOp",EDGE,"E23.27.4"),sQuery(id+"F3.wireOp",EDGE,"E23.28.0"),sQuery(id+"F3.wireOp",EDGE,"E23.28.1"),sQuery(id+"F3.wireOp",EDGE,"E23.28.2"),sQuery(id+"F3.wireOp",EDGE,"E23.28.3"),sQuery(id+"F3.wireOp",EDGE,"E23.28.4"),sQuery(id+"F3.wireOp",EDGE,"E23.29.0"),sQuery(id+"F3.wireOp",EDGE,"E23.29.1"),sQuery(id+"F3.wireOp",EDGE,"E23.29.2"),sQuery(id+"F3.wireOp",EDGE,"E23.29.3"),sQuery(id+"F3.wireOp",EDGE,"E23.29.4")])]});
            transform(context, id + "F6", {"entities" : qUnion([Q0]), "transformType" : TransformType.TRANSLATION_3D, "dx" : 0 * mm, "dy" : 0 * mm, "dz" : 8 * mm, "makeCopy" : true});
        }
        {
            var Q0;
            Q0=makeQuery(id+"F3.imprint","IMPRINT",FACE,{"disambiguationData":[TD([[makeQuery(id+"F3.imprint","IMPRINT",EDGE,{"derivedFrom":sQuery(id+"F3.wireOp",EDGE,"E1")}),1.0]])]});
            var Q1;
            Q1=makeQuery(id+"F3.imprint","IMPRINT",FACE,{"disambiguationData":[TD([[makeQuery(id+"F3.imprint","IMPRINT",EDGE,{"derivedFrom":sQuery(id+"F3.wireOp",EDGE,"E2")}),1.0]])]});
            extrude(context, id + "F7", {"entities" : qUnion([Q0, Q1]), "depth" : 12 * mm});
        }
        {
            var Q0;
            Q0=makeQuery(id+"F3.imprint","IMPRINT",FACE,{"disambiguationData":[TD([[makeQuery(id+"F3.imprint","IMPRINT",EDGE,{"derivedFrom":sQuery(id+"F3.wireOp",EDGE,"E2")}),1.0]])]});
            extrude(context, id + "F8", {"entities" : qUnion([Q0]), "operationType" : NewBodyOperationType.ADD, "depth" : (getVariable(context, 'e') + getVariable(context, 'h1') + getVariable(context, 'h2')) * mm});
        }
        {
            var Q0;
            Q0=qCreatedBy(makeId("Front.planeOp"),FACE);
            var sketch = newSketch(context, id + "F9", { "sketchPlane" : qUnion([Q0])});
            skLineSegment(sketch, "E24", {"start": v(0, 0) * mm, "end": v(0, 17.5) * mm, "construction": true});
            skLineSegment(sketch, "E25", {"start": v(-4.9, 6) * mm, "end": v(-4.9, 12.5) * mm});
            skLineSegment(sketch, "E26", {"start": v(4.9, 20.5) * mm, "end": v(4.9, 6) * mm});
            skLineSegment(sketch, "E27.bottom", {"start": v(4.9, 20.5) * mm, "end": v(5.15, 20.5) * mm, "construction": true});
            skLineSegment(sketch, "E27.top", {"start": v(4.9, 19) * mm, "end": v(5.15, 19) * mm, "construction": true});
            skLineSegment(sketch, "E27.left", {"start": v(4.9, 20.5) * mm, "end": v(4.9, 19) * mm, "construction": true});
            skLineSegment(sketch, "E27.right", {"start": v(5.15, 20.5) * mm, "end": v(5.15, 19) * mm, "construction": true});
            skPoint(sketch, "E28", {"position": v(5.15, 19.75) * mm});
            skLineSegment(sketch, "E29", {"start": v(4.9, 20.5) * mm, "end": v(5.15, 19.75) * mm});
            skLineSegment(sketch, "E30", {"start": v(5.15, 19.75) * mm, "end": v(4.9, 19) * mm});
            skLineSegment(sketch, "E31", {"start": v(4.9, 19) * mm, "end": v(4.9, 20.5) * mm});
            skSolve(sketch);
        }
        {
            var Q0;
            Q0=makeQuery(id+"F9.imprint","IMPRINT",FACE,{"disambiguationData":[TD([[makeQuery(id+"F9.imprint","IMPRINT",EDGE,{"derivedFrom":sQuery(id+"F9.wireOp",EDGE,"E29")}),-1.0]])]});
            var Q1;
            Q1=sQuery(id+"F9.wireOp",EDGE,"E24");
            revolve(context, id + "F10", {"operationType" : NewBodyOperationType.ADD, "entities" : qUnion([Q0]), "axis" : qUnion([Q1]), "revolveType" : RevolveType.FULL});
        }
        {
            var Q0;
            Q0=makeQuery(id+"F8.opExtrude","CAP_FACE",FACE,{"disambiguationData":[OSD([sQuery(id+"F3.wireOp",EDGE,"E2"),sQuery(id+"F3.wireOp",EDGE,"E3"),sQuery(id+"F3.wireOp",EDGE,"E4.bottom"),sQuery(id+"F3.wireOp",EDGE,"E4.top"),sQuery(id+"F3.wireOp",EDGE,"E5.trimOffspring")])],"isStart":false});
            cPlane(context, id + "F11", {"entities" : qUnion([Q0]), "cplaneType" : CPlaneType.OFFSET, "offset" : 0 * mm, "width" : 150 * mm, "height" : 150 * mm});
        }
        {
            var Q0;
            Q0=qCreatedBy(id+"F11.planeOp",FACE);
            var sketch = newSketch(context, id + "F12", { "sketchPlane" : qUnion([Q0])});
            skArc(sketch, "E32", {"start": v(-2.38, 2.7) * mm, "mid": v(-3.6, 0) * mm, "end": v(-2.38, -2.7) * mm});
            skLineSegment(sketch, "E33.bottom", {"start": v(-2.38, 2.7) * mm, "end": v(2.38, 2.7) * mm});
            skLineSegment(sketch, "E33.top", {"start": v(-2.38, -2.7) * mm, "end": v(2.38, -2.7) * mm});
            skPoint(sketch, "E34.orphan", {"position": v(4.18, 2.7) * mm});
            skPoint(sketch, "E35.orphan", {"position": v(3.52, -2.7) * mm});
            skArc(sketch, "E36.trimOffspring", {"start": v(2.38, -2.7) * mm, "mid": v(3.6, 0) * mm, "end": v(2.38, 2.7) * mm});
            skPoint(sketch, "E37.orphan", {"position": v(-4.18, -2.7) * mm});
            skPoint(sketch, "E38.orphan", {"position": v(-3.52, 2.7) * mm});
            skSolve(sketch);
        }
    });
